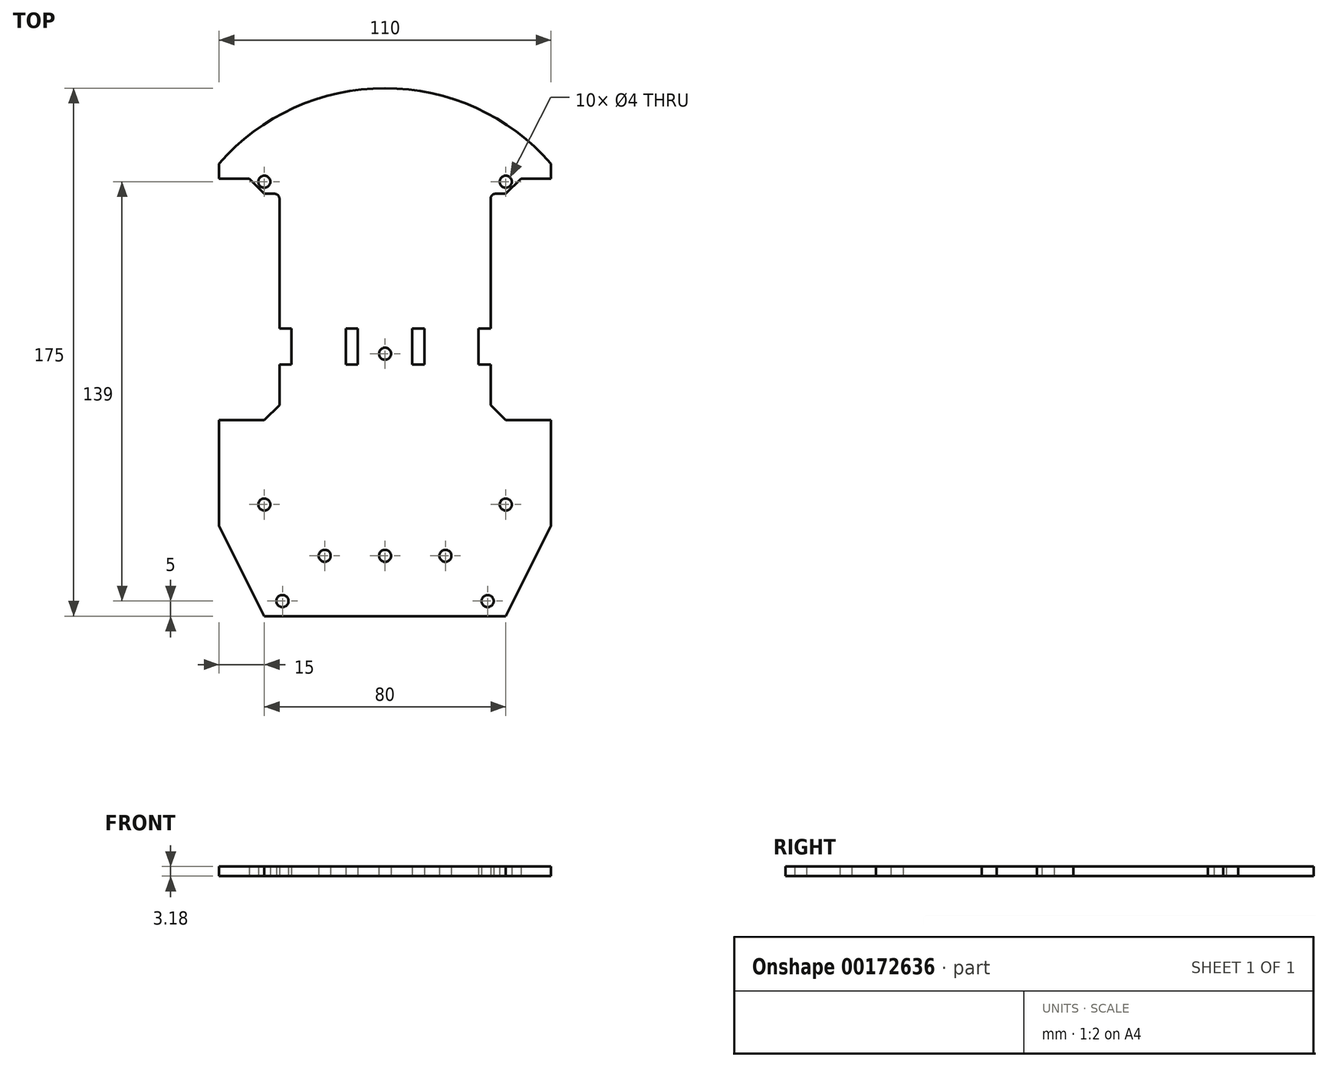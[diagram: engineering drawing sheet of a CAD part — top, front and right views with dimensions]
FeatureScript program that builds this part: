
annotation { "Feature Type Name" : "Feature", "Feature Type Description" : "" }
export const myFeature = defineFeature(function(context is Context, id is Id, definition is map)
    precondition{}
    {
        {
            var Q0;
            Q0=qCreatedBy(makeId("Top.planeOp"),FACE);
            var sketch = newSketch(context, id + "F0", { "sketchPlane" : qUnion([Q0])});
            skLineSegment(sketch, "E0.top", {"start": v(-40, -87.5) * mm, "end": v(40, -87.5) * mm});
            skLineSegment(sketch, "E0.left", {"start": v(-55, 62.5) * mm, "end": v(-55, 57.5) * mm});
            skLineSegment(sketch, "E0.right", {"start": v(55, 62.5) * mm, "end": v(55, 57.5) * mm});
            skPoint(sketch, "E0.middle", {"position": v(0, 0) * mm});
            skPoint(sketch, "E1", {"position": v(0, -87.5) * mm});
            skPoint(sketch, "E2", {"position": v(-40, -87.5) * mm});
            skPoint(sketch, "E3", {"position": v(40, -87.5) * mm});
            skLineSegment(sketch, "E4", {"start": v(-55, -57.5) * mm, "end": v(-40, -87.5) * mm});
            skLineSegment(sketch, "E5", {"start": v(55, -57.5) * mm, "end": v(40, -87.5) * mm});
            skPoint(sketch, "E6", {"position": v(0, 87.5) * mm});
            skArc(sketch, "E7", {"start": v(55, 62.5) * mm, "mid": v(0, 87.5) * mm, "end": v(-55, 62.5) * mm});
            skPoint(sketch, "E8", {"position": v(-34, -82.5) * mm});
            skCircle(sketch, "E9", {"center": v(-34, -82.5) * mm, "radius": 2 * mm});
            skPoint(sketch, "E10", {"position": v(-40, 56.5) * mm});
            skLineSegment(sketch, "E11", {"start": v(-55, 62.5) * mm, "end": v(-16.67, 62.5) * mm, "construction": true});
            skCircle(sketch, "E12", {"center": v(-40, 56.5) * mm, "radius": 2 * mm});
            skCircle(sketch, "E13.MirrorC", {"center": v(40, 56.5) * mm, "radius": 2 * mm});
            skCircle(sketch, "E14.MirrorC", {"center": v(34, -82.5) * mm, "radius": 2 * mm});
            skPoint(sketch, "E15", {"position": v(0, -0.5) * mm});
            skCircle(sketch, "E16", {"center": v(0, -0.5) * mm, "radius": 2 * mm});
            skPoint(sketch, "E17", {"position": v(55, -22.5) * mm});
            skPoint(sketch, "E18", {"position": v(55, 57.5) * mm});
            skLineSegment(sketch, "E19", {"start": v(55, 57.5) * mm, "end": v(45, 57.5) * mm});
            skLineSegment(sketch, "E20", {"start": v(45, 57.5) * mm, "end": v(40, 52.5) * mm});
            skLineSegment(sketch, "E21", {"start": v(40, 52.5) * mm, "end": v(36.62, 52.5) * mm});
            skLineSegment(sketch, "E22", {"start": v(55, -22.5) * mm, "end": v(40, -22.5) * mm});
            skLineSegment(sketch, "E23", {"start": v(40, -22.5) * mm, "end": v(35, -17.5) * mm});
            skLineSegment(sketch, "E24", {"start": v(35, -17.5) * mm, "end": v(35, -4.12) * mm});
            skLineSegment(sketch, "E25.MirrorCS", {"start": v(-55, 57.5) * mm, "end": v(-45, 57.5) * mm});
            skLineSegment(sketch, "E26.MirrorCS", {"start": v(-45, 57.5) * mm, "end": v(-40, 52.5) * mm});
            skLineSegment(sketch, "E27.MirrorCS", {"start": v(-40, 52.5) * mm, "end": v(-36.62, 52.5) * mm});
            skLineSegment(sketch, "E28.MirrorCS", {"start": v(-35, -17.5) * mm, "end": v(-35, -4.12) * mm});
            skLineSegment(sketch, "E29.MirrorCS", {"start": v(-40, -22.5) * mm, "end": v(-35, -17.5) * mm});
            skLineSegment(sketch, "E30.MirrorCS", {"start": v(-55, -22.5) * mm, "end": v(-40, -22.5) * mm});
            skPoint(sketch, "E31.visualSharp", {"position": v(35, 52.5) * mm});
            skArc(sketch, "E31.filletArc", {"start": v(36.62, 52.5) * mm, "mid": v(35.48, 52.02) * mm, "end": v(35, 50.88) * mm});
            skPoint(sketch, "E32.visualSharp", {"position": v(-35, 52.5) * mm});
            skArc(sketch, "E32.filletArc", {"start": v(-35, 50.88) * mm, "mid": v(-35.48, 52.02) * mm, "end": v(-36.62, 52.5) * mm});
            skLineSegment(sketch, "E33.trimOffspring", {"start": v(55, -22.5) * mm, "end": v(55, -57.5) * mm});
            skLineSegment(sketch, "E34.trimOffspring", {"start": v(-55, -22.5) * mm, "end": v(-55, -57.5) * mm});
            skPoint(sketch, "E35", {"position": v(20, -67.5) * mm});
            skCircle(sketch, "E36", {"center": v(20, -67.5) * mm, "radius": 2 * mm});
            skCircle(sketch, "E37.MirrorC", {"center": v(-20, -67.5) * mm, "radius": 2 * mm});
            skPoint(sketch, "E38", {"position": v(35, -4.12) * mm});
            skPoint(sketch, "E39", {"position": v(35, 7.87) * mm});
            skLineSegment(sketch, "E40.bottom", {"start": v(35, 7.87) * mm, "end": v(31, 7.87) * mm});
            skLineSegment(sketch, "E40.top", {"start": v(35, -4.12) * mm, "end": v(31, -4.12) * mm});
            skLineSegment(sketch, "E40.right", {"start": v(31, 7.87) * mm, "end": v(31, -4.12) * mm});
            skPoint(sketch, "E41", {"position": v(13, 7.87) * mm});
            skLineSegment(sketch, "E42.bottom", {"start": v(13, 7.87) * mm, "end": v(9, 7.87) * mm});
            skLineSegment(sketch, "E42.top", {"start": v(13, -4.12) * mm, "end": v(9, -4.12) * mm});
            skLineSegment(sketch, "E42.left", {"start": v(13, 7.87) * mm, "end": v(13, -4.12) * mm});
            skLineSegment(sketch, "E42.right", {"start": v(9, 7.87) * mm, "end": v(9, -4.12) * mm});
            skLineSegment(sketch, "E43.MirrorCS", {"start": v(-9, 7.87) * mm, "end": v(-9, -4.12) * mm});
            skLineSegment(sketch, "E44.MirrorCS", {"start": v(-13, 7.87) * mm, "end": v(-9, 7.87) * mm});
            skLineSegment(sketch, "E45.MirrorCS", {"start": v(-13, 7.87) * mm, "end": v(-13, -4.12) * mm});
            skLineSegment(sketch, "E46.MirrorCS", {"start": v(-13, -4.12) * mm, "end": v(-9, -4.12) * mm});
            skLineSegment(sketch, "E47.MirrorCS", {"start": v(-31, 7.87) * mm, "end": v(-31, -4.12) * mm});
            skLineSegment(sketch, "E48.MirrorCS", {"start": v(-35, -4.12) * mm, "end": v(-31, -4.12) * mm});
            skLineSegment(sketch, "E49.MirrorCS", {"start": v(-35, 7.87) * mm, "end": v(-31, 7.87) * mm});
            skLineSegment(sketch, "E50.trimOffspring", {"start": v(35, 7.87) * mm, "end": v(35, 50.88) * mm});
            skLineSegment(sketch, "E51.trimOffspring", {"start": v(-35, 7.87) * mm, "end": v(-35, 50.88) * mm});
            skPoint(sketch, "E52", {"position": v(0, -67.5) * mm});
            skCircle(sketch, "E53", {"center": v(0, -67.5) * mm, "radius": 2 * mm});
            skPoint(sketch, "E54", {"position": v(-40, -50.5) * mm});
            skCircle(sketch, "E55", {"center": v(-40, -50.5) * mm, "radius": 2 * mm});
            skCircle(sketch, "E56.MirrorC", {"center": v(40, -50.5) * mm, "radius": 2 * mm});
            skSolve(sketch);
        }
        {
            var Q0;
            Q0=qSketchRegion(id+"F0",true);
            extrude(context, id + "F1", {"entities" : qUnion([Q0]), "depth" : 3.17 * mm});
        }
    });
